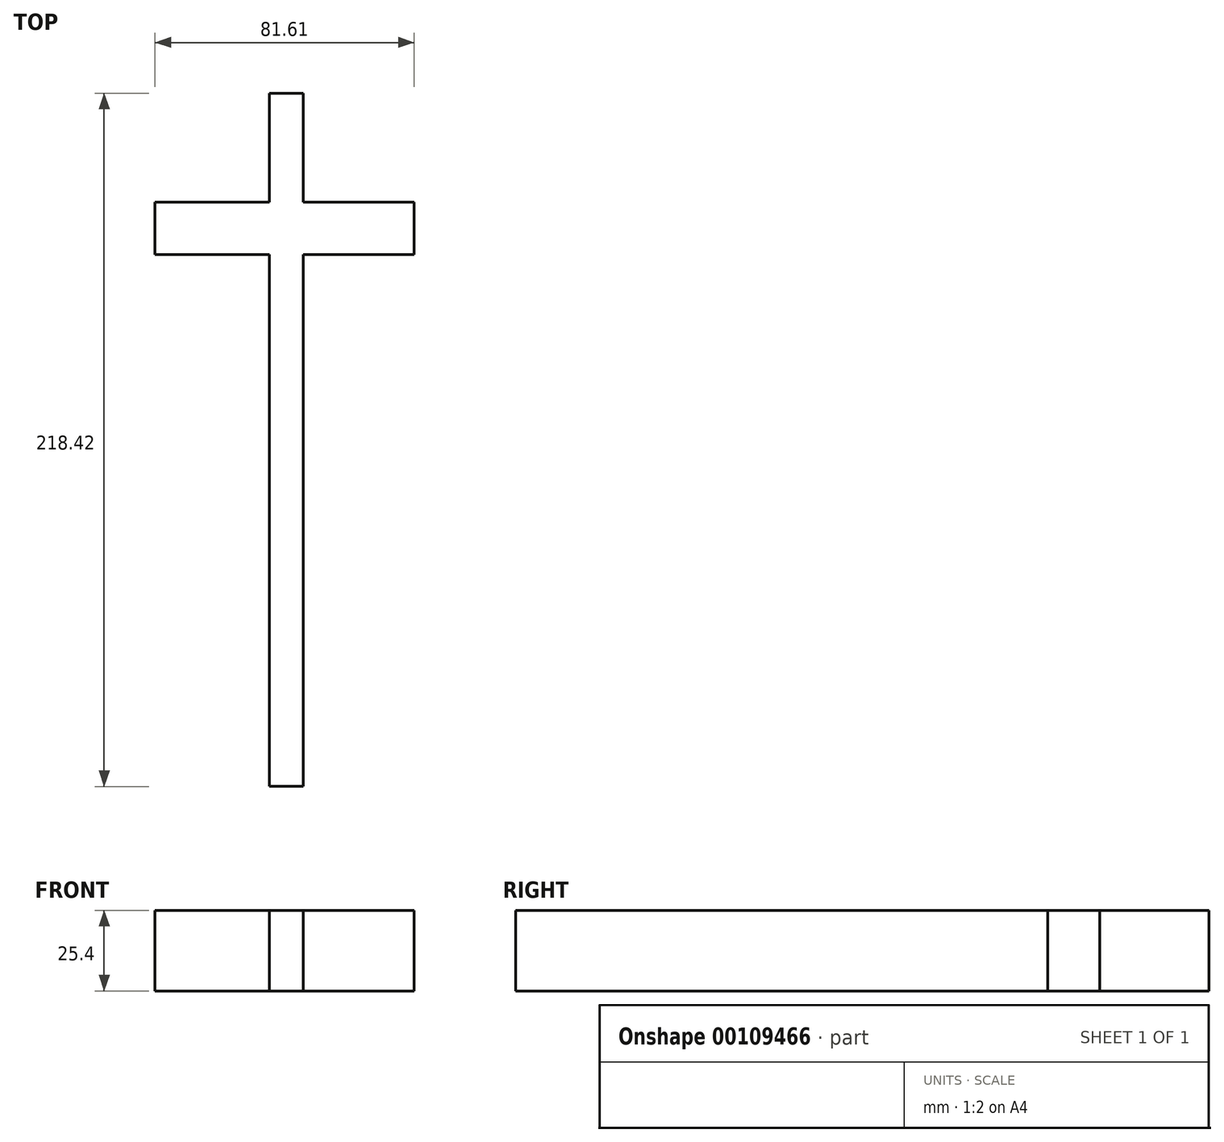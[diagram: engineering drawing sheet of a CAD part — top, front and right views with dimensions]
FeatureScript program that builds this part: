
annotation { "Feature Type Name" : "Feature", "Feature Type Description" : "" }
export const myFeature = defineFeature(function(context is Context, id is Id, definition is map)
    precondition{}
    {
        {
            var Q0;
            Q0=qCreatedBy(makeId("Top.planeOp"),FACE);
            var sketch = newSketch(context, id + "F0", { "sketchPlane" : qUnion([Q0])});
            skLineSegment(sketch, "E0.bottom", {"start": v(-17.15, 50.81) * mm, "end": v(-27.76, 50.81) * mm});
            skLineSegment(sketch, "E0.top", {"start": v(-17.15, -167.6) * mm, "end": v(-27.76, -167.6) * mm});
            skLineSegment(sketch, "E0.left", {"start": v(-17.15, 50.81) * mm, "end": v(-17.15, -167.6) * mm});
            skLineSegment(sketch, "E0.right", {"start": v(-27.76, 50.81) * mm, "end": v(-27.76, -167.6) * mm});
            skLineSegment(sketch, "E1.bottom", {"start": v(-63.8, 16.44) * mm, "end": v(17.8, 16.44) * mm});
            skLineSegment(sketch, "E1.top", {"start": v(-63.8, 0) * mm, "end": v(17.8, 0) * mm});
            skLineSegment(sketch, "E1.left", {"start": v(-63.8, 16.44) * mm, "end": v(-63.8, 0) * mm});
            skLineSegment(sketch, "E1.right", {"start": v(17.8, 16.44) * mm, "end": v(17.8, 0) * mm});
            skSolve(sketch);
        }
        {
            var Q0;
            Q0 = qSketchRegion(id + "F0", true);
            extrude(context, id + "F1", {"entities" : qUnion([Q0]), "depth" : 25.4 * mm});
        }
    });
